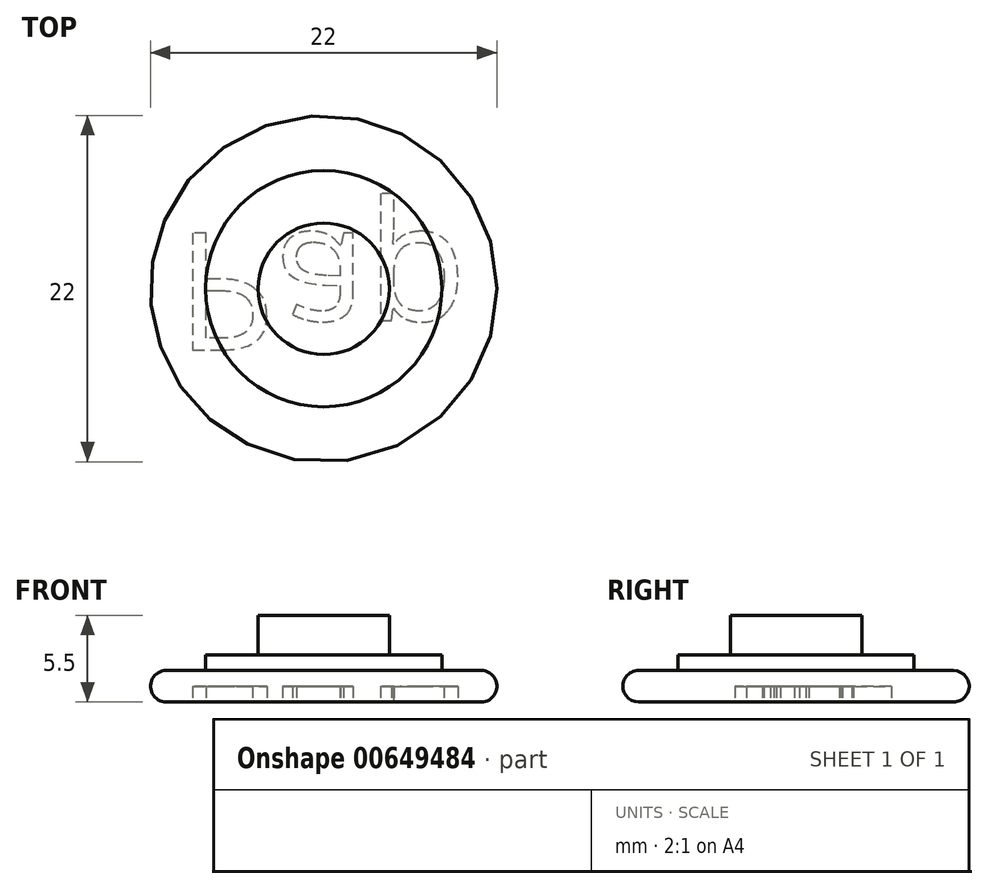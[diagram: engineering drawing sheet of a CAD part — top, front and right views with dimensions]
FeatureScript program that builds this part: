
annotation { "Feature Type Name" : "Feature", "Feature Type Description" : "" }
export const myFeature = defineFeature(function(context is Context, id is Id, definition is map)
    precondition{}
    {
        {
            var Q0;
            Q0=qCreatedBy(makeId("Top.planeOp"),FACE);
            var sketch = newSketch(context, id + "F0", { "sketchPlane" : qUnion([Q0])});
            skCircle(sketch, "E0", {"center": v(0, 0) * mm, "radius": 11 * mm});
            skCircle(sketch, "E1", {"center": v(0, 0) * mm, "radius": 7.5 * mm});
            skCircle(sketch, "E2", {"center": v(0, 0) * mm, "radius": 4.17 * mm});
            skSolve(sketch);
        }
        {
            var Q0;
            Q0=makeQuery(id+"F0.imprint","IMPRINT",FACE,{"disambiguationData":[TD([[makeQuery(id+"F0.imprint","IMPRINT",EDGE,{"derivedFrom":sQuery(id+"F0.wireOp",EDGE,"E0")}),1.0]])]});
            extrude(context, id + "F1", {"entities" : qUnion([Q0]), "depth" : 2 * mm, "offsetDistance" : 25 * mm});
        }
        {
            var Q0;
            Q0=makeQuery(id+"F0.imprint","IMPRINT",FACE,{"disambiguationData":[TD([[makeQuery(id+"F0.imprint","IMPRINT",EDGE,{"derivedFrom":sQuery(id+"F0.wireOp",EDGE,"E1")}),1.0]])]});
            extrude(context, id + "F2", {"entities" : qUnion([Q0]), "operationType" : NewBodyOperationType.ADD, "depth" : 3 * mm, "offsetDistance" : 25 * mm});
        }
        {
            var Q0;
            Q0=makeQuery(id+"F0.imprint","IMPRINT",FACE,{"disambiguationData":[TD([[makeQuery(id+"F0.imprint","IMPRINT",EDGE,{"derivedFrom":sQuery(id+"F0.wireOp",EDGE,"E2")}),1.0]])]});
            extrude(context, id + "F3", {"entities" : qUnion([Q0]), "operationType" : NewBodyOperationType.ADD, "depth" : 5.5 * mm, "offsetDistance" : 25 * mm});
        }
        {
            var Q0;
            Q0=makeQuery(id+"F1.opExtrude","CAP_EDGE",EDGE,{"disambiguationData":[OSD([sQuery(id+"F0.wireOp",EDGE,"E0")])],"isStart":false});
            var Q1;
            Q1=makeQuery(id+"F1.opExtrude","CAP_EDGE",EDGE,{"disambiguationData":[OSD([sQuery(id+"F0.wireOp",EDGE,"E0")])],"isStart":true});
            fillet(context, id + "F4", {"entities" : qUnion([Q0, Q1]), "radius" : 1 * mm, "tangentPropagation" : true, "allowEdgeOverflow" : false});
        }
        {
            var Q0;
            {var subQ0=sQuery(id+"F0.wireOp",EDGE,"E2");var subQ1=sQuery(id+"F0.wireOp",EDGE,"E1");Q0=makeQuery(id+"F3.boolean.opBoolean","MERGE",FACE,{"derivedFrom":[makeQuery(id+"F2.boolean.opBoolean","MERGE",FACE,{"derivedFrom":[makeQuery(id+"F1.opExtrude","CAP_FACE",FACE,{"disambiguationData":[OSD([sQuery(id+"F0.wireOp",EDGE,"E0"),subQ1])],"isStart":true}),makeQuery(id+"F2.opExtrude","CAP_FACE",FACE,{"disambiguationData":[OSD([subQ1,subQ0])],"isStart":true})]}),makeQuery(id+"F3.opExtrude","CAP_FACE",FACE,{"disambiguationData":[OSD([subQ0])],"isStart":true})]});}
            var sketch = newSketch(context, id + "F5", { "sketchPlane" : qUnion([Q0])});
            skText(sketch, "E3", { "text": "Pap", "fontName": "OpenSans-Regular.ttf"});
            const initialGuessF5  = {"E3": [-0.00935, -0.00355, 1, 0, 0.0075]};
            skSetInitialGuess(sketch, initialGuessF5);
            skSolve(sketch);
        }
        {
            var Q0;
            Q0 = qSketchRegion(id + "F5", true);
            extrude(context, id + "F6", {"entities" : qUnion([Q0]), "operationType" : NewBodyOperationType.REMOVE, "oppositeDirection" : true, "depth" : 1 * mm, "offsetDistance" : 25 * mm});
        }
    });
